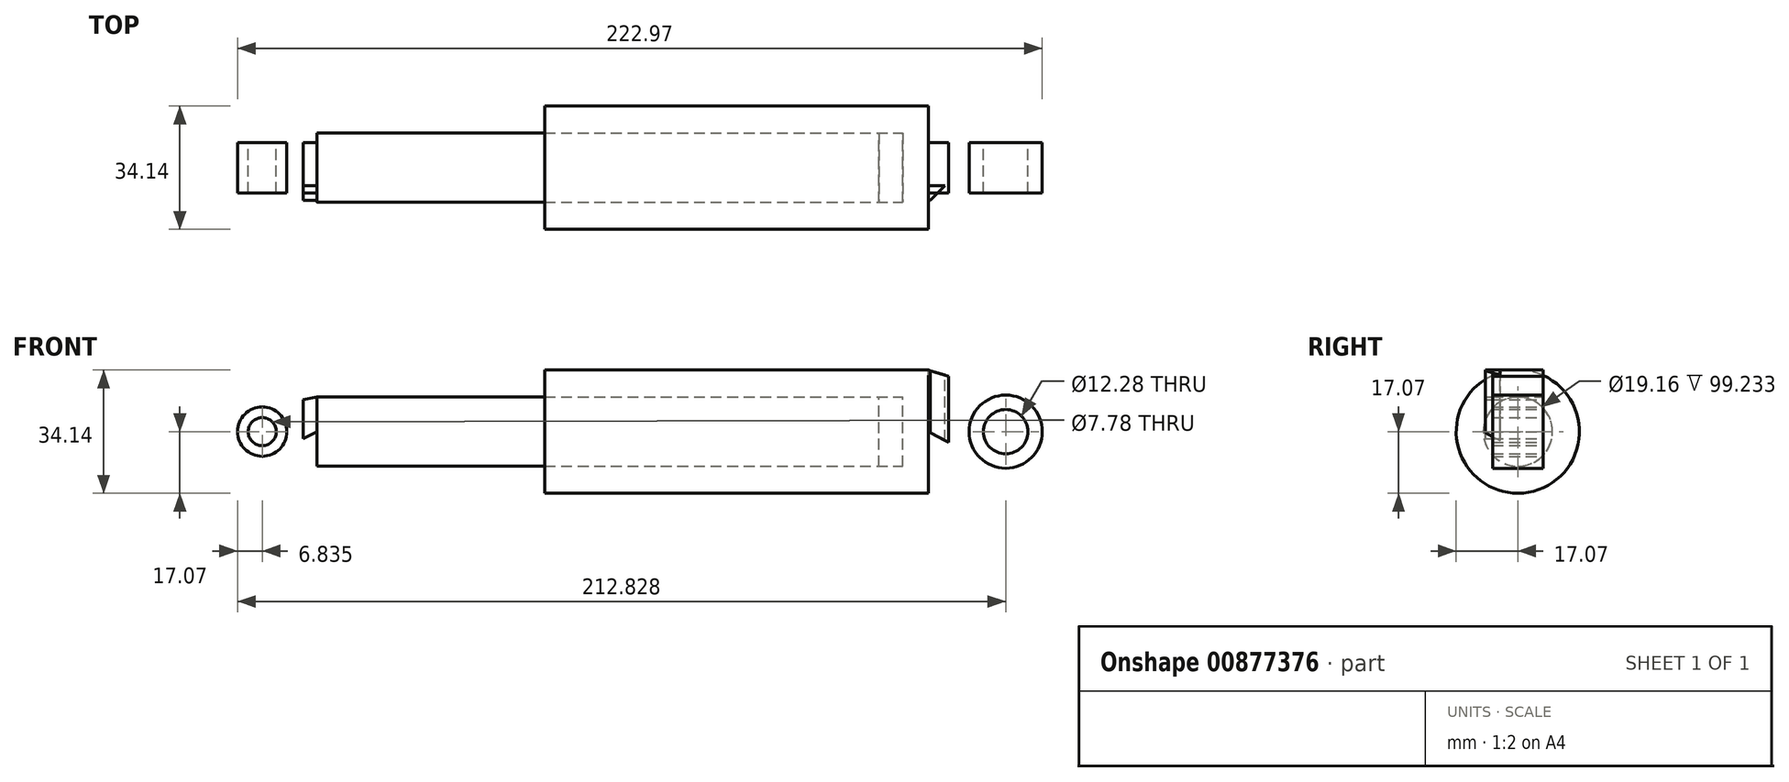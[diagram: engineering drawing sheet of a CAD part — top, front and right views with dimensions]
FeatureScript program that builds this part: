
annotation { "Feature Type Name" : "Feature", "Feature Type Description" : "" }
export const myFeature = defineFeature(function(context is Context, id is Id, definition is map)
    precondition{}
    {
        {
            var Q0;
            Q0=qCreatedBy(makeId("Front.planeOp"),FACE);
            var sketch = newSketch(context, id + "F0", { "sketchPlane" : qUnion([Q0])});
            skLineSegment(sketch, "E0", {"start": v(-88.05, 0) * mm, "end": v(-88.05, 9.58) * mm});
            skLineSegment(sketch, "E1", {"start": v(-88.05, 9.58) * mm, "end": v(67.61, 9.58) * mm});
            skLineSegment(sketch, "E2", {"start": v(67.61, 9.58) * mm, "end": v(67.61, 0) * mm});
            skLineSegment(sketch, "E3", {"start": v(67.61, 0) * mm, "end": v(-88.05, 0) * mm});
            skLineSegment(sketch, "E4", {"start": v(-25, 9.58) * mm, "end": v(-25, 17.07) * mm});
            skLineSegment(sketch, "E5", {"start": v(-25, 17.07) * mm, "end": v(81.28, 17.07) * mm});
            skLineSegment(sketch, "E6", {"start": v(81.28, 17.07) * mm, "end": v(81.28, 0) * mm});
            skLineSegment(sketch, "E7", {"start": v(81.28, 0) * mm, "end": v(74.23, 0) * mm});
            skLineSegment(sketch, "E8", {"start": v(74.23, 0) * mm, "end": v(74.23, 9.58) * mm});
            skLineSegment(sketch, "E9", {"start": v(74.23, 9.58) * mm, "end": v(-25, 9.58) * mm});
            skCircle(sketch, "E10", {"center": v(-103.24, 0) * mm, "radius": 6.84 * mm});
            skCircle(sketch, "E11", {"center": v(102.76, 0) * mm, "radius": 10.14 * mm});
            skLineSegment(sketch, "E12", {"start": v(-104.4, 6.74) * mm, "end": v(-88.05, 9.58) * mm});
            skLineSegment(sketch, "E13", {"start": v(-100.16, -6.1) * mm, "end": v(-88.05, 0) * mm});
            skLineSegment(sketch, "E14", {"start": v(81.28, 17.07) * mm, "end": v(105.69, 9.7) * mm});
            skLineSegment(sketch, "E15", {"start": v(81.28, 0) * mm, "end": v(97.97, -8.94) * mm});
            skCircle(sketch, "E16", {"center": v(-103.24, 0) * mm, "radius": 3.89 * mm});
            skCircle(sketch, "E17", {"center": v(102.76, 0) * mm, "radius": 6.14 * mm});
            skLineSegment(sketch, "E18", {"start": v(-91.84, 8.92) * mm, "end": v(-91.84, -1.9) * mm});
            skLineSegment(sketch, "E19", {"start": v(86.89, 15.38) * mm, "end": v(86.89, -3) * mm});
            skSolve(sketch);
        }
        {
            var Q0;
            {var subQ0=sQuery(id+"F0.wireOp",EDGE,"E4");Q0=makeQuery(id+"F0.imprint","IMPRINT",FACE,{"disambiguationData":[TD([[makeQuery(id+"F0.imprint","IMPRINT",EDGE,{"derivedFrom":subQ0}),-1.0]])]});}
            var Q1;
            Q1=sQuery(id+"F0.wireOp",EDGE,"E3");
            revolve(context, id + "F1", {"surfaceOperationType" : NewSurfaceOperationType.NEW, "entities" : qUnion([Q0]), "axis" : qUnion([Q1]), "revolveType" : RevolveType.FULL});
        }
        {
            var Q0;
            Q0=makeQuery(id+"F0.imprint","IMPRINT",FACE,{"disambiguationData":[TD([[makeQuery(id+"F0.imprint","IMPRINT",EDGE,{"derivedFrom":sQuery(id+"F0.wireOp",EDGE,"E0")}),-1.0]])]});
            var Q1;
            Q1=sQuery(id+"F0.wireOp",EDGE,"E3");
            revolve(context, id + "F2", {"surfaceOperationType" : NewSurfaceOperationType.NEW, "entities" : qUnion([Q0]), "axis" : qUnion([Q1]), "revolveType" : RevolveType.FULL});
        }
        {
            var Q0;
            Q0=makeQuery(id+"F0.imprint","IMPRINT",FACE,{"disambiguationData":[TD([[makeQuery(id+"F0.imprint","IMPRINT",EDGE,{"derivedFrom":sQuery(id+"F0.wireOp",EDGE,"E0")}),1.0]])]});
            var Q1;
            Q1=makeQuery(id+"F0.imprint","IMPRINT",FACE,{"disambiguationData":[TD([[makeQuery(id+"F0.imprint","IMPRINT",EDGE,{"derivedFrom":sQuery(id+"F0.wireOp",EDGE,"E16")}),-1.0]])]});
            var Q2;
            Q2=makeQuery(id+"F0.imprint","IMPRINT",FACE,{"disambiguationData":[TD([[makeQuery(id+"F0.imprint","IMPRINT",EDGE,{"derivedFrom":sQuery(id+"F0.wireOp",EDGE,"E6")}),1.0]])]});
            var Q3;
            Q3=makeQuery(id+"F0.imprint","IMPRINT",FACE,{"disambiguationData":[TD([[makeQuery(id+"F0.imprint","IMPRINT",EDGE,{"derivedFrom":sQuery(id+"F0.wireOp",EDGE,"E17")}),-1.0]])]});
            extrude(context, id + "F3", {"entities" : qUnion([Q0, Q1, Q2, Q3]), "operationType" : NewBodyOperationType.ADD, "endBound" : BoundingType.SYMMETRIC, "depth" : 14 * mm, "offsetDistance" : 25 * mm});
        }
        {
            var Q0;
            Q0=makeQuery(id+"F3.opExtrude","CAP_FACE",FACE,{"disambiguationData":[OSD([sQuery(id+"F0.wireOp",EDGE,"E6"),sQuery(id+"F0.wireOp",EDGE,"E14"),sQuery(id+"F0.wireOp",EDGE,"E15"),sQuery(id+"F0.wireOp",EDGE,"E19")])],"isStart":false});
            var Q1;
            Q1=makeQuery(id+"F3.opExtrude","CAP_FACE",FACE,{"disambiguationData":[OSD([sQuery(id+"F0.wireOp",EDGE,"E0"),sQuery(id+"F0.wireOp",EDGE,"E12"),sQuery(id+"F0.wireOp",EDGE,"E13"),sQuery(id+"F0.wireOp",EDGE,"E18")])],"isStart":false});
            extrude(context, id + "F4", {"entities" : qUnion([Q0, Q1]), "endBound" : BoundingType.SYMMETRIC, "depth" : 4 * mm, "offsetDistance" : 25 * mm});
        }
        {
            var Q0;
            Q0=makeQuery(id+"F4.opExtrude","CAP_EDGE",EDGE,{"disambiguationData":[OSD([sQuery(id+"F0.wireOp",EDGE,"E19")])],"isStart":false});
            chamfer(context, id + "F5", {"entities" : qUnion([Q0]), "width" : 5 * mm, "tangentPropagation" : true});
        }
    });
